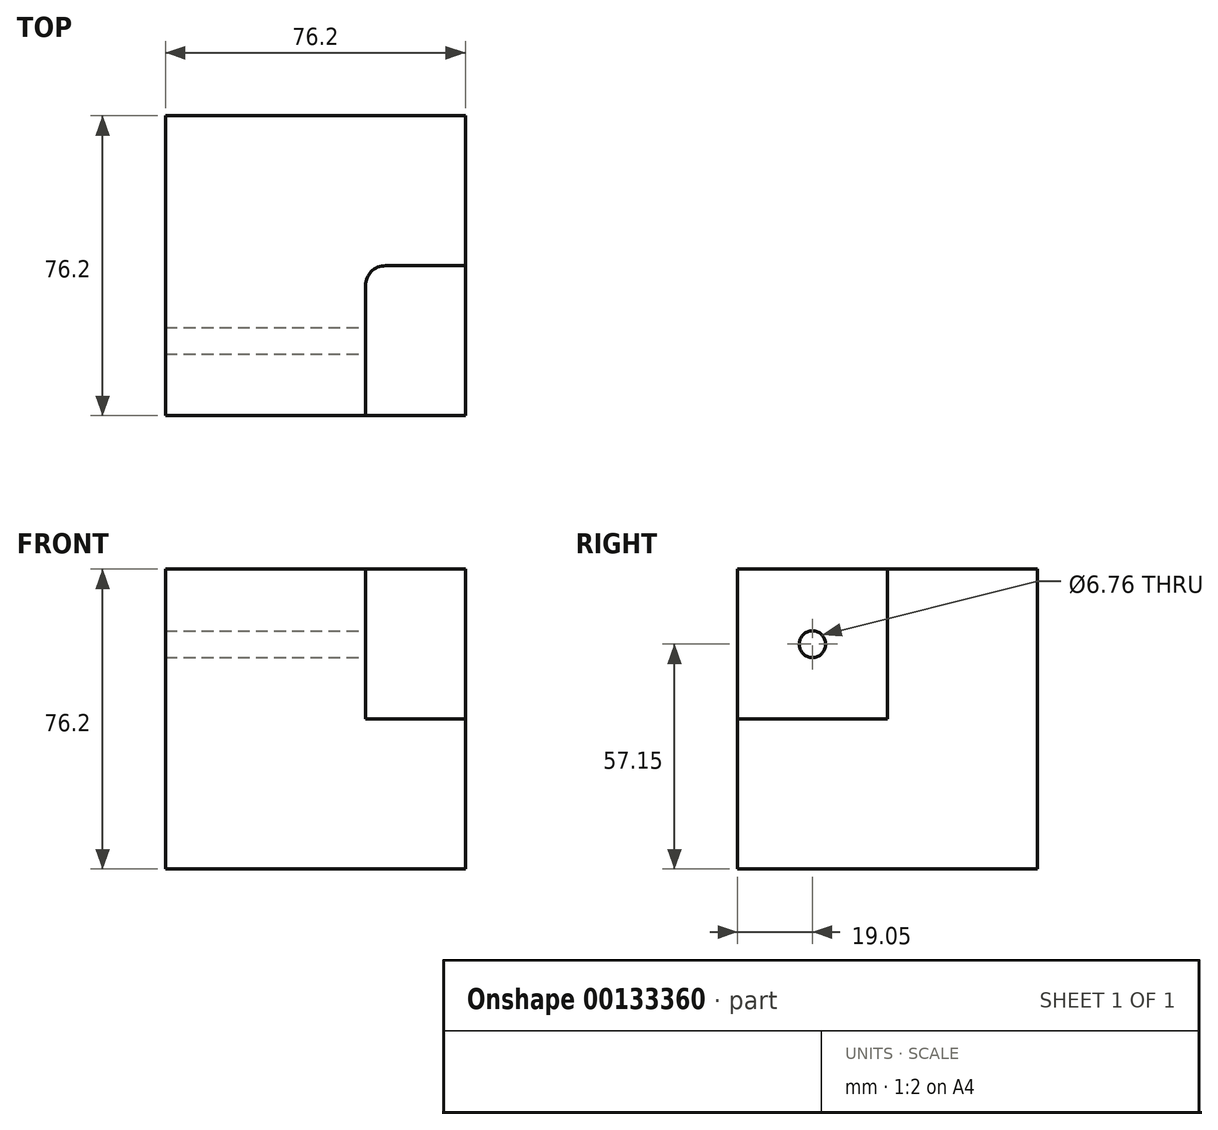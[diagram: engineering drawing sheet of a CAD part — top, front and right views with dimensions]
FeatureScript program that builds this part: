
annotation { "Feature Type Name" : "Feature", "Feature Type Description" : "" }
export const myFeature = defineFeature(function(context is Context, id is Id, definition is map)
    precondition{}
    {
        {
            var Q0;
            Q0=qCreatedBy(makeId("Front.planeOp"),FACE);
            var sketch = newSketch(context, id + "F0", { "sketchPlane" : qUnion([Q0])});
            skLineSegment(sketch, "E0.bottom", {"start": v(38.1, 38.1) * mm, "end": v(-38.1, 38.1) * mm});
            skLineSegment(sketch, "E0.top", {"start": v(38.1, -38.1) * mm, "end": v(-38.1, -38.1) * mm});
            skLineSegment(sketch, "E0.left", {"start": v(38.1, 38.1) * mm, "end": v(38.1, -38.1) * mm});
            skLineSegment(sketch, "E0.right", {"start": v(-38.1, 38.1) * mm, "end": v(-38.1, -38.1) * mm});
            skPoint(sketch, "E0.middle", {"position": v(0, 0) * mm});
            skSolve(sketch);
        }
        {
            var Q0;
            Q0 = qSketchRegion(id + "F0", true);
            extrude(context, id + "F1", {"entities" : qUnion([Q0]), "endBound" : BoundingType.SYMMETRIC, "depth" : 76.2 * mm});
        }
        {
            var Q0;
            Q0=makeQuery(id+"F1.opExtrude","CAP_FACE",FACE,{"disambiguationData":[OSD([sQuery(id+"F0.wireOp",EDGE,"E0.bottom"),sQuery(id+"F0.wireOp",EDGE,"E0.top"),sQuery(id+"F0.wireOp",EDGE,"E0.left"),sQuery(id+"F0.wireOp",EDGE,"E0.right")])],"isStart":false});
            var sketch = newSketch(context, id + "F2", { "sketchPlane" : qUnion([Q0])});
            skLineSegment(sketch, "E1.bottom", {"start": v(38.1, 38.1) * mm, "end": v(12.7, 38.1) * mm});
            skLineSegment(sketch, "E1.top", {"start": v(38.1, 0) * mm, "end": v(12.7, 0) * mm});
            skLineSegment(sketch, "E1.left", {"start": v(38.1, 38.1) * mm, "end": v(38.1, 0) * mm});
            skLineSegment(sketch, "E1.right", {"start": v(12.7, 38.1) * mm, "end": v(12.7, 0) * mm});
            skSolve(sketch);
        }
        {
            var Q0;
            Q0 = qSketchRegion(id + "F2", true);
            extrude(context, id + "F3", {"entities" : qUnion([Q0]), "operationType" : NewBodyOperationType.REMOVE, "oppositeDirection" : true, "depth" : 38.1 * mm});
        }
        {
            var Q0;
            Q0=makeQuery(id+"F3.boolean.opBoolean","COPY",FACE,{"derivedFrom":makeQuery(id+"F3.opExtrude","SWEPT_FACE",FACE,{"disambiguationData":[OSD([sQuery(id+"F2.wireOp",EDGE,"E1.right")])]})});
            var sketch = newSketch(context, id + "F4", { "sketchPlane" : qUnion([Q0])});
            skPoint(sketch, "E2", {"position": v(-19.05, 19.05) * mm});
            skPoint(sketch, "E2.positionSnap0", {"position": v(-38.1, 19.05) * mm});
            skPoint(sketch, "E2.positionSnap1", {"position": v(-19.05, 38.1) * mm});
            skSolve(sketch);
        }
        {
            var Q0;
            Q0=sQuery(id+"F4.wireOp",VERTEX,"E2");
            var Q1;
            Q1=makeQuery(id+"F1.opExtrude","SWEPT_BODY",BODY,{"disambiguationData":[OSD([sQuery(id+"F0.wireOp",EDGE,"E0.bottom"),sQuery(id+"F0.wireOp",EDGE,"E0.top"),sQuery(id+"F0.wireOp",EDGE,"E0.left"),sQuery(id+"F0.wireOp",EDGE,"E0.right")])]});
            hole(context, id + "F5", {"style" : HoleStyle.SIMPLE, "endStyle" : HoleEndStyle.THROUGH, "standardTappedOrClearance" : lookupTablePath({ "standard" : "ANSI", "fit" : "Normal (ASME)", "size" : "1/4", "type" : "Clearance" }), "standardBlindInLast" : lookupTablePath({ "fit" : "Free", "standard" : "ANSI", "size" : "1/4", "type" : "Clearance" }), "holeDiameter" : 6.76 * mm, "locations" : qUnion([Q0]), "scope" : qUnion([Q1]), "isTappedThrough" : true});
        }
        {
            var Q0;
            Q0=makeQuery(id+"F3.boolean.opBoolean","COPY",EDGE,{"derivedFrom":makeQuery(id+"F3.opExtrude","CAP_EDGE",EDGE,{"disambiguationData":[OSD([sQuery(id+"F2.wireOp",EDGE,"E1.right")])],"isStart":false})});
            fillet(context, id + "F6", {"entities" : qUnion([Q0]), "radius" : 5.08 * mm, "tangentPropagation" : true, "allowEdgeOverflow" : false});
        }
    });
